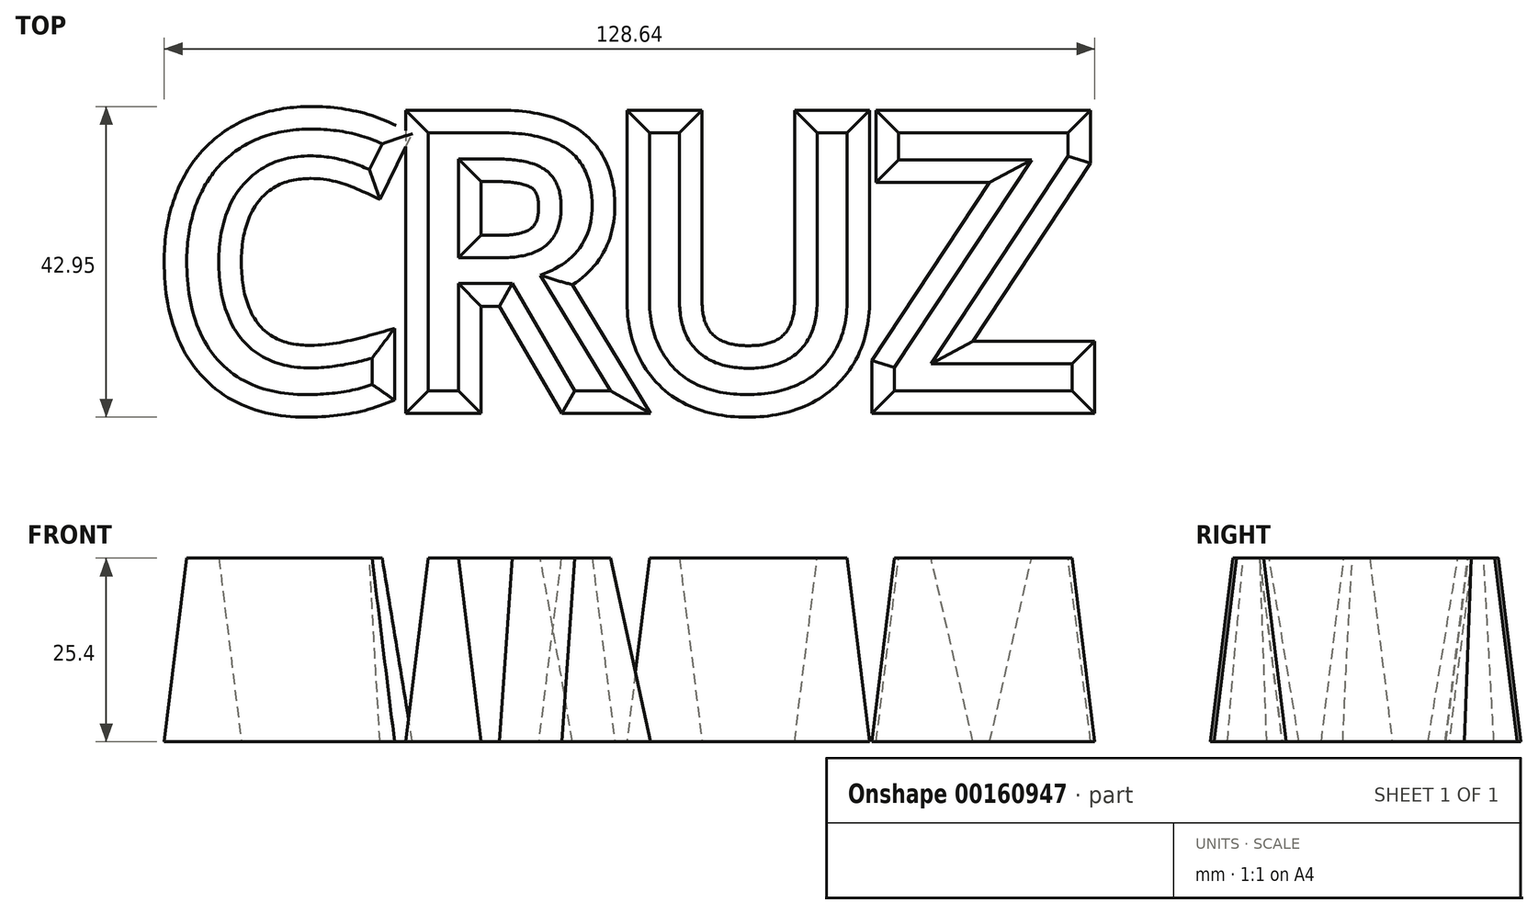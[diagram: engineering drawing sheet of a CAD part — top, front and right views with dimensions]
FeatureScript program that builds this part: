
annotation { "Feature Type Name" : "Feature", "Feature Type Description" : "" }
export const myFeature = defineFeature(function(context is Context, id is Id, definition is map)
    precondition{}
    {
        {
            var Q0;
            Q0=qCreatedBy(makeId("Top.planeOp"),FACE);
            var sketch = newSketch(context, id + "F0", { "sketchPlane" : qUnion([Q0])});
            skText(sketch, "E0", { "text": "CRUZ", "fontName": "OpenSans-Regular.ttf"});
            const initialGuessF0  = {"E0": [-0.0598, 0.01074, 1, 0, 0.03602]};
            skSetInitialGuess(sketch, initialGuessF0);
            skSolve(sketch);
        }
        {
            var Q0;
            Q0 = qSketchRegion(id + "F0", true);
            extrude(context, id + "F1", {"entities" : qUnion([Q0]), "oppositeDirection" : true, "depth" : 25.4 * mm, "hasDraft" : true, "draftAngle" : 7 * degree});
        }
    });
